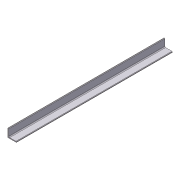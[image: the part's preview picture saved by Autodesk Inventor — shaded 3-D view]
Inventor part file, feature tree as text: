
AUTODESK INVENTOR PART (.ipt)
format: ipt  version: 2012 (Build 160160000, 160)  size: 76,288 bytes
history: native  units: in
note: dims shown in document units (in); Inventor stores cm internally (conversion verified against a paired STEP export)
features: extrude x1, sketch x1
ambient origin geometry x8: Origin, YZ Plane, XZ Plane, XY Plane, X Axis, Y Axis, Z Axis, Center Point
bodies: Solid1 (feature_tree)
feature tree (2):
  extrude  "Extrusion1"  Depth=0.25in
  sketch  "Sketch1"  dims[d0=2.5in d1=0.25in d2=0.25in d3=0.125in d4=46.5in d5=0.0in]
